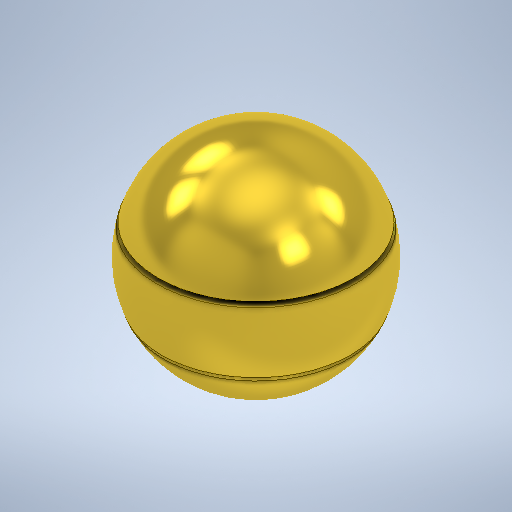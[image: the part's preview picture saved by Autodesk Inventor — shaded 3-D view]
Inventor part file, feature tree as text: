
AUTODESK INVENTOR PART (.ipt)
format: ipt  version: 2025.2 (Build 292293000, 293)  size: 309,760 bytes
history: native  units: mm
features: other x3, sketch x1
ambient origin geometry x8: Origin, YZ Plane, XZ Plane, XY Plane, X Axis, Y Axis, Z Axis, Center Point
bodies: Body1 (feature_tree)
feature tree (4):
  other  "Sólido1"
  sketch  "Esboço1"  dims[d0=20.0mm d4=360.0deg d6=2.0mm d7=25.0mm d8=0.5mm d9=0.5mm d10=180.0deg d5=0.872665mm d11=0.872665mm]
  other  "Revolução1"
  other  "Revolução2"
